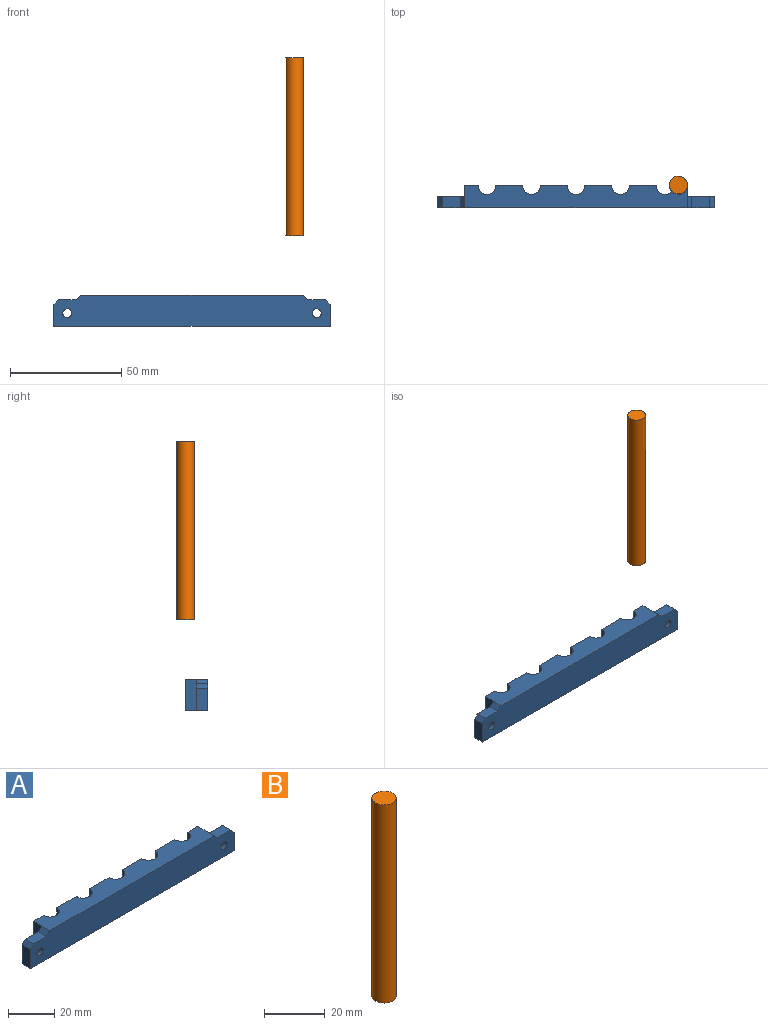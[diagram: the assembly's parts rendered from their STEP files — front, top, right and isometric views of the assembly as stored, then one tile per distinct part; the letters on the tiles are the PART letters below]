
ASSEMBLY  parts=2 mates=1
PART A: 50 faces, bbox 124x10x14 mm
  f0: plane 14x5mm, normal (-1,0,0), area 70mm2, adj f4,f6,f9,f39
  f1: plane 18x9mm, normal (0,0,-1), area 70.7mm2, adj f2,f4,f7,f8
  f2: plane 14x12mm, normal (0,1,0), area 108mm2, adj f1,f3,f6,f7,f8,f9,f10,f31
  f3: cylinder r=4mm len=14mm, axis (0,0,-1), area 175.9mm2, adj f2,f4,f6,f9
  f4: plane 14x6mm, normal (0,1,0), area 54mm2, adj f0,f1,f3,f6,f7,f8,f9,f10
  f5: plane 124x14mm, normal (0,-1,0), area 1662.9mm2, adj f6,f9,f36,f37,f38,f40,f41,f42
  f6: plane 100x10mm, normal (0,0,1), area 874.3mm2, adj f0,f2,f3,f4,f5,f12,f13,f14
  f7: cylinder r=9mm len=18mm, axis (0,0,-1), area 282.7mm2, adj f1,f2,f4,f10
  f8: cylinder r=6mm len=12mm, axis (0,0,-1), area 188.5mm2, adj f1,f2,f4,f10
  f9: plane 124x10mm, normal (0,0,-1), area 994.3mm2, adj f0,f2,f3,f4,f5,f12,f13,f14
  f10: plane 18x9mm, normal (0,0,1), area 70.7mm2, adj f2,f4,f7,f8
  f11: plane 18x9mm, normal (0,0,-1), area 70.7mm2, adj f12,f14,f15,f16
  f12: plane 14x12mm, normal (0,1,0), area 108mm2, adj f6,f9,f11,f13,f15,f16,f17,f18
  f13: cylinder r=4mm len=14mm, axis (0,0,-1), area 175.9mm2, adj f6,f9,f12,f14
  f14: plane 14x12mm, normal (0,1,0), area 108mm2, adj f6,f9,f11,f13,f15,f16,f17,f31
  f15: cylinder r=9mm len=18mm, axis (0,0,-1), area 282.7mm2, adj f11,f12,f14,f17
  f16: cylinder r=6mm len=12mm, axis (0,0,-1), area 188.5mm2, adj f11,f12,f14,f17
  f17: plane 18x9mm, normal (0,0,1), area 70.7mm2, adj f12,f14,f15,f16
  f18: plane 18x9mm, normal (0,0,-1), area 70.7mm2, adj f12,f19,f21,f22
  f19: plane 14x12mm, normal (0,1,0), area 108mm2, adj f6,f9,f18,f20,f21,f22,f23,f24
  f20: cylinder r=4mm len=14mm, axis (0,0,-1), area 175.9mm2, adj f6,f9,f12,f19
  f21: cylinder r=9mm len=18mm, axis (0,0,-1), area 282.7mm2, adj f12,f18,f19,f23
  f22: cylinder r=6mm len=12mm, axis (0,0,-1), area 188.5mm2, adj f12,f18,f19,f23
  f23: plane 18x9mm, normal (0,0,1), area 70.7mm2, adj f12,f19,f21,f22
  f24: plane 18x9mm, normal (0,0,-1), area 70.7mm2, adj f19,f25,f28,f29
  f25: plane 14x6mm, normal (0,1,0), area 54mm2, adj f6,f9,f24,f26,f27,f28,f29,f30
  f26: cylinder r=4mm len=14mm, axis (0,0,-1), area 175.9mm2, adj f6,f9,f19,f25
  f27: plane 14x5mm, normal (1,0,0), area 70mm2, adj f6,f9,f25,f43
  f28: cylinder r=9mm len=18mm, axis (0,0,-1), area 282.7mm2, adj f19,f24,f25,f30
  f29: cylinder r=6mm len=12mm, axis (0,0,-1), area 188.5mm2, adj f19,f24,f25,f30
  f30: plane 18x9mm, normal (0,0,1), area 70.7mm2, adj f19,f25,f28,f29
  f31: plane 18x9mm, normal (0,0,-1), area 70.7mm2, adj f2,f14,f33,f34
  f32: cylinder r=4mm len=14mm, axis (0,0,-1), area 175.9mm2, adj f2,f6,f9,f14
  f33: cylinder r=9mm len=18mm, axis (0,0,-1), area 282.7mm2, adj f2,f14,f31,f35
  f34: cylinder r=6mm len=12mm, axis (0,0,-1), area 188.5mm2, adj f2,f14,f31,f35
  f35: plane 18x9mm, normal (0,0,1), area 70.7mm2, adj f2,f14,f33,f34
  f36: plane 8x5mm, normal (0,0,1), area 40mm2, adj f5,f39,f44,f45
  f37: plane 10x5mm, normal (-1,0,0), area 50mm2, adj f5,f9,f39,f44
  f38: cylinder r=2mm len=4mm, axis (0,-1,0), area 25.1mm2, adj f5,f49
  f39: plane 14x12mm, normal (0,1,0), area 65.5mm2, adj f0,f9,f36,f37,f44,f45,f49
  f40: plane 10x5mm, normal (1,0,0), area 50mm2, adj f5,f9,f43,f47
  f41: plane 8x5mm, normal (0,0,1), area 40mm2, adj f5,f43,f46,f47
  f42: cylinder r=2mm len=4mm, axis (0,-1,0), area 25.1mm2, adj f5,f48
  f43: plane 14x12mm, normal (0,1,0), area 65.5mm2, adj f9,f27,f40,f41,f46,f47,f48
  f44: plane 5x2mm, normal (-0.71,0,0.71), area 14.1mm2, adj f5,f36,f37,f39
  f45: plane 5x2mm, normal (-0.71,0,0.71), area 14.1mm2, adj f5,f6,f36,f39
  f46: plane 5x2mm, normal (0.71,0,0.71), area 14.1mm2, adj f5,f6,f41,f43
  f47: plane 5x2mm, normal (0.71,0,0.71), area 14.1mm2, adj f5,f40,f41,f43
  f48: cone r=2mm half-angle=45deg, axis (0,1,0), area 93.3mm2, adj f42,f43
  f49: cone r=5mm half-angle=45deg, axis (0,1,0), area 93.3mm2, adj f38,f39
PART B: 3 faces, bbox 8x8x80 mm
  f0: cylinder r=4mm len=80mm, axis (0,0,-1), area 2010.6mm2, adj f1,f2
  f1: plane 8x8mm, normal (0,0,1), area 50.3mm2, adj f0
  f2: plane 8x8mm, normal (0,0,-1), area 50.3mm2, adj f0
PLACE A t=(4.36,-7.45,0)mm fixed
PLACE B rot(axis=(1,0,0),180deg) t=(90.36,2.55,113.81)mm
MATE slider B.f0 <-> A.f24  axis (0,0,-1) through (90.36,2.55,73.81)mm
